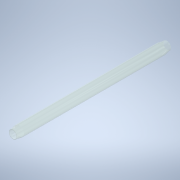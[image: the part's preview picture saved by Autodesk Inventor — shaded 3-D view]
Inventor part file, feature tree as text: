
AUTODESK INVENTOR PART (.ipt)
format: ipt  version: 2020 (Build 240168000, 168)  size: 137,216 bytes
history: native  units: mm
features: sketch x2, extrude x1, revolve x1, fillet x1, mirror x1
ambient origin geometry x8: Origin, YZ Plane, XZ Plane, XY Plane, X Axis, Y Axis, Z Axis, Center Point
bodies: Solid1 (feature_tree)
feature tree (6):
  extrude  "Extrusion1"  Depth=2.0mm
  revolve  "Revolution1"  [1 undecoded]
  fillet  "Fillet2"  Radius=2.0mm
  mirror  "Mirror1"
  sketch  "Sketch1"  dims[d0=30.0mm d1=2.0mm]
  sketch  "Sketch2"  dims[d2=476.0mm d3=0.0mm d4=2.0mm d5=2.0mm d8=12.0mm d10=5.0mm d11=90.0deg d13=20.0mm d14=1.0mm]
note: 1 required parameter value undecoded (feature->parameter linkage not recoverable at this tier; creation-order binding heuristic only, values carry confidence <= 0.55)
